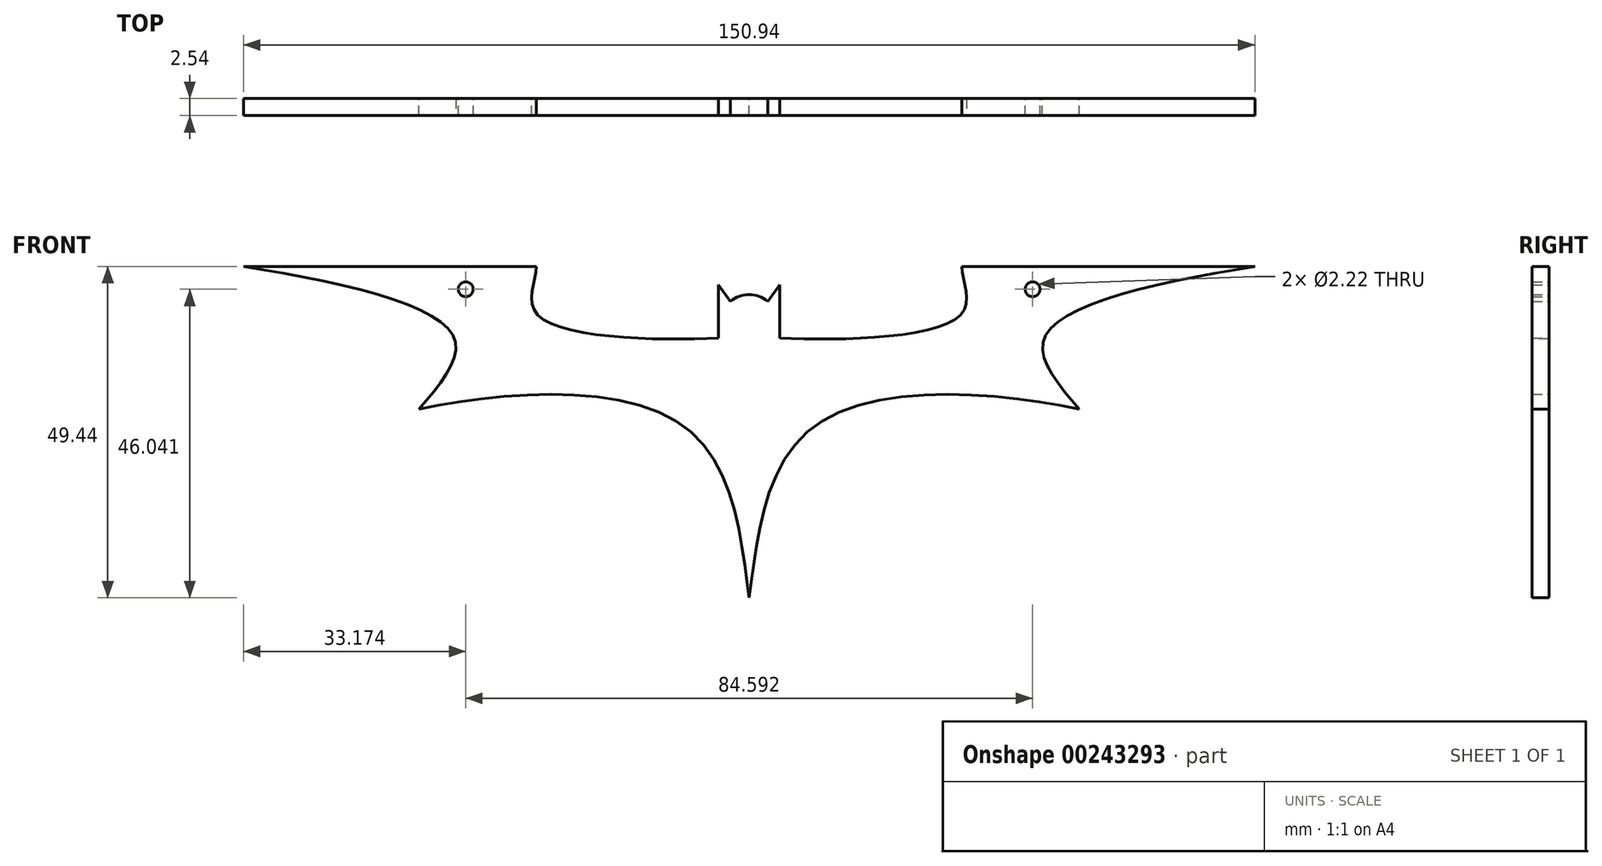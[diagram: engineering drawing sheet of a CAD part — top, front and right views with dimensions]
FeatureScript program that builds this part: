
annotation { "Feature Type Name" : "Feature", "Feature Type Description" : "" }
export const myFeature = defineFeature(function(context is Context, id is Id, definition is map)
    precondition{}
    {
        {
            var Q0;
            Q0=qCreatedBy(makeId("Front.planeOp"),FACE);
            var sketch = newSketch(context, id + "F0", { "sketchPlane" : qUnion([Q0])});
            skLineSegment(sketch, "E0", {"start": v(-4.56, 0) * mm, "end": v(-4.56, 7.91) * mm});
            skPoint(sketch, "E1.endSnap0", {"position": v(-4.56, 3.96) * mm});
            skFitSpline(sketch, "E2", {"points": [v(-4.56, 0) * mm, v(-31.72, 3.63) * mm, v(-31.75, 10.67) * mm], "startDerivative": vector(-37.95, -1.9) * mm, "endDerivative": vector(0.3, 19.05) * mm});
            skFitSpline(sketch, "E3", {"points": [v(-49.27, -10.65) * mm, v(-9.57, -13.3) * mm, v(0, -38.77) * mm], "startDerivative": vector(62.92, 13.8) * mm, "endDerivative": vector(7.33, -52.9) * mm});
            skFitSpline(sketch, "E4.MirrorCS", {"points": [v(4.56, 0) * mm, v(31.72, 3.63) * mm, v(31.75, 10.67) * mm], "startDerivative": vector(37.95, -1.9) * mm, "endDerivative": vector(-0.3, 19.05) * mm});
            skFitSpline(sketch, "E5.MirrorCS", {"points": [v(49.27, -10.65) * mm, v(9.57, -13.3) * mm, v(0, -38.77) * mm], "startDerivative": vector(-62.92, 13.8) * mm, "endDerivative": vector(-7.33, -52.9) * mm});
            skLineSegment(sketch, "E6.MirrorCS", {"start": v(4.56, 0) * mm, "end": v(4.56, 7.91) * mm});
            skArc(sketch, "E7", {"start": v(2.8, 5.43) * mm, "mid": v(0, 6.46) * mm, "end": v(-2.8, 5.43) * mm});
            skLineSegment(sketch, "E8", {"start": v(-4.56, 7.91) * mm, "end": v(-2.8, 5.43) * mm});
            skLineSegment(sketch, "E9.MirrorCS", {"start": v(4.56, 7.91) * mm, "end": v(2.8, 5.43) * mm});
            skArc(sketch, "E10.MirrorC", {"start": v(-2.8, 5.43) * mm, "mid": v(-1.5, 6.2) * mm, "end": v(0, 6.46) * mm});
            skPoint(sketch, "E11.start.orphan", {"position": v(0, 8) * mm});
            skCircle(sketch, "E12", {"center": v(-42.3, 7.27) * mm, "radius": 1.1 * mm});
            skCircle(sketch, "E13.MirrorC", {"center": v(42.3, 7.27) * mm, "radius": 1.1 * mm});
            skLineSegment(sketch, "E14", {"start": v(31.75, 10.67) * mm, "end": v(75.47, 10.67) * mm});
            skFitSpline(sketch, "E15", {"points": [v(49.27, -10.65) * mm, v(44.04, 0) * mm, v(75.47, 10.67) * mm], "startDerivative": vector(-26, 30.8) * mm, "endDerivative": vector(70.39, 11.4) * mm});
            skFitSpline(sketch, "E16.MirrorCS", {"points": [v(-49.27, -10.65) * mm, v(-44.04, 0) * mm, v(-75.47, 10.67) * mm], "startDerivative": vector(26, 30.8) * mm, "endDerivative": vector(-70.39, 11.4) * mm});
            skLineSegment(sketch, "E17.MirrorCS", {"start": v(-31.75, 10.67) * mm, "end": v(-75.47, 10.67) * mm});
            skSolve(sketch);
        }
        {
            var Q0;
            Q0=makeQuery(id+"F0.imprint","IMPRINT",FACE,{"disambiguationData":[TD([[makeQuery(id+"F0.imprint","IMPRINT",EDGE,{"derivedFrom":sQuery(id+"F0.wireOp",EDGE,"E0")}),-1.0]])]});
            extrude(context, id + "F1", {"entities" : qUnion([Q0]), "depth" : 2.54 * mm});
        }
    });
